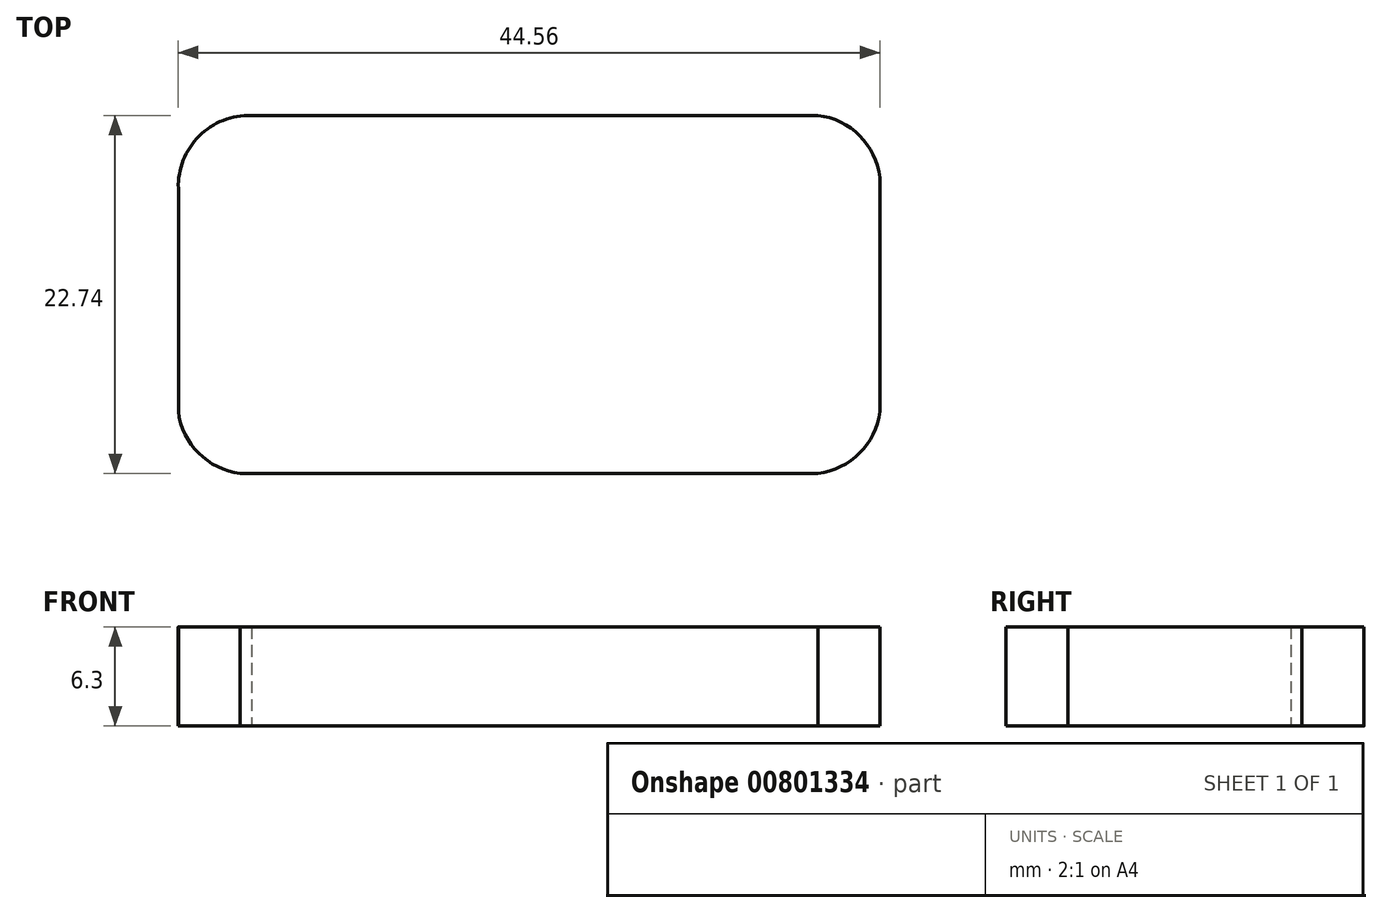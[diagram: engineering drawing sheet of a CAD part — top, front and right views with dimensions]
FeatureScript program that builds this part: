
annotation { "Feature Type Name" : "Feature", "Feature Type Description" : "" }
export const myFeature = defineFeature(function(context is Context, id is Id, definition is map)
    precondition{}
    {
        {
            var Q0;
            Q0=qCreatedBy(makeId("Top.planeOp"),FACE);
            var sketch = newSketch(context, id + "F0", { "sketchPlane" : qUnion([Q0])});
            skLineSegment(sketch, "E0.bottom", {"start": v(-17.64, 11.37) * mm, "end": v(18.34, 11.37) * mm});
            skLineSegment(sketch, "E0.top", {"start": v(-18.34, -11.37) * mm, "end": v(18.34, -11.37) * mm});
            skLineSegment(sketch, "E0.left", {"start": v(-22.28, 6.73) * mm, "end": v(-22.28, -7.43) * mm});
            skLineSegment(sketch, "E0.right", {"start": v(22.28, 7.43) * mm, "end": v(22.28, -7.43) * mm});
            skPoint(sketch, "E0.middle", {"position": v(0, 0) * mm});
            skArc(sketch, "E1", {"start": v(-17.64, 11.37) * mm, "mid": v(-20.96, 10.05) * mm, "end": v(-22.28, 6.73) * mm});
            skPoint(sketch, "E2.orphan", {"position": v(-22.28, 11.37) * mm});
            skArc(sketch, "E3", {"start": v(22.28, 7.43) * mm, "mid": v(21, 10.08) * mm, "end": v(18.34, 11.37) * mm});
            skArc(sketch, "E4", {"start": v(18.34, -11.37) * mm, "mid": v(21, -10.08) * mm, "end": v(22.28, -7.43) * mm});
            skArc(sketch, "E5", {"start": v(-22.28, -7.43) * mm, "mid": v(-21, -10.08) * mm, "end": v(-18.34, -11.37) * mm});
            skPoint(sketch, "E6.orphan", {"position": v(-22.28, -11.37) * mm});
            skPoint(sketch, "E7.orphan", {"position": v(22.28, 11.37) * mm});
            skPoint(sketch, "E8.orphan", {"position": v(22.28, -11.37) * mm});
            skSolve(sketch);
        }
        {
            var Q0;
            Q0=makeQuery(id+"F0.imprint","IMPRINT",FACE,{"disambiguationData":[TD([[makeQuery(id+"F0.imprint","IMPRINT",EDGE,{"derivedFrom":sQuery(id+"F0.wireOp",EDGE,"E0.bottom")}),-1.0]])]});
            extrude(context, id + "F1", {"entities" : qUnion([Q0]), "depth" : 6.3 * mm, "offsetDistance" : 25 * mm});
        }
    });
